# Revit family: FU_Modular_Sandler_Tetris Bench
name_source: partatom
category: Furniture
units: mm (PartAtom-declared; Revit-internal decimal feet)

## family parameters
Always vertical = Yes
Cut with Voids When Loaded = No
OmniClass Number = 23.40.20.00
OmniClass Title = General Furniture and Specialties
Room Calculation Point = No
Shared = No
Work Plane-Based = No

## types (6) — shared parameters
Depth = 800 mm  [stored 2.62467 ft]
Frame = Epoxy - M1_B00 - Black
Height = 425 mm  [stored 1.39436 ft]
Manufacturer = Sandler
Seat = Fabric - Mainline Flax - Upminster MLF20
URL = https://www.sandlerseating.com
zero-valued in all types: Default Elevation

## per-type parameters (varying)
| type | Description | Width |
| Tetris 8060 | Upholstered modular seat W.78.7″ with steel plate legs. | 2000 mm  [stored 6.56168 ft] |
| Tetris 8010 | Upholstered modular seat W.23.6″ with steel plate legs. | 600 mm |
| Tetris 8020 | Upholstered modular seat W.31.5″ with steel plate legs. | 800 mm  [stored 2.62467 ft] |
| Tetris 8030 | Upholstered modular seat W.39.4″ with steel plate legs. | 1000 mm  [stored 3.28084 ft] |
| Tetris 8040 | Upholstered modular seat W.47.2″ with steel plate legs. | 1200 mm |
| Tetris 8050 | Upholstered modular seat W.63″ with steel plate legs. | 1600 mm  [stored 5.24934 ft] |

note: column(s) folded — value = type name in every type: Model

note: [stored X ft] marks values corroborated as IEEE doubles in the binary element streams (Revit-internal decimal feet)

## geometry (parser evidence)
native form markers: Sweep x3
no freeform markers — native parametric forms only
